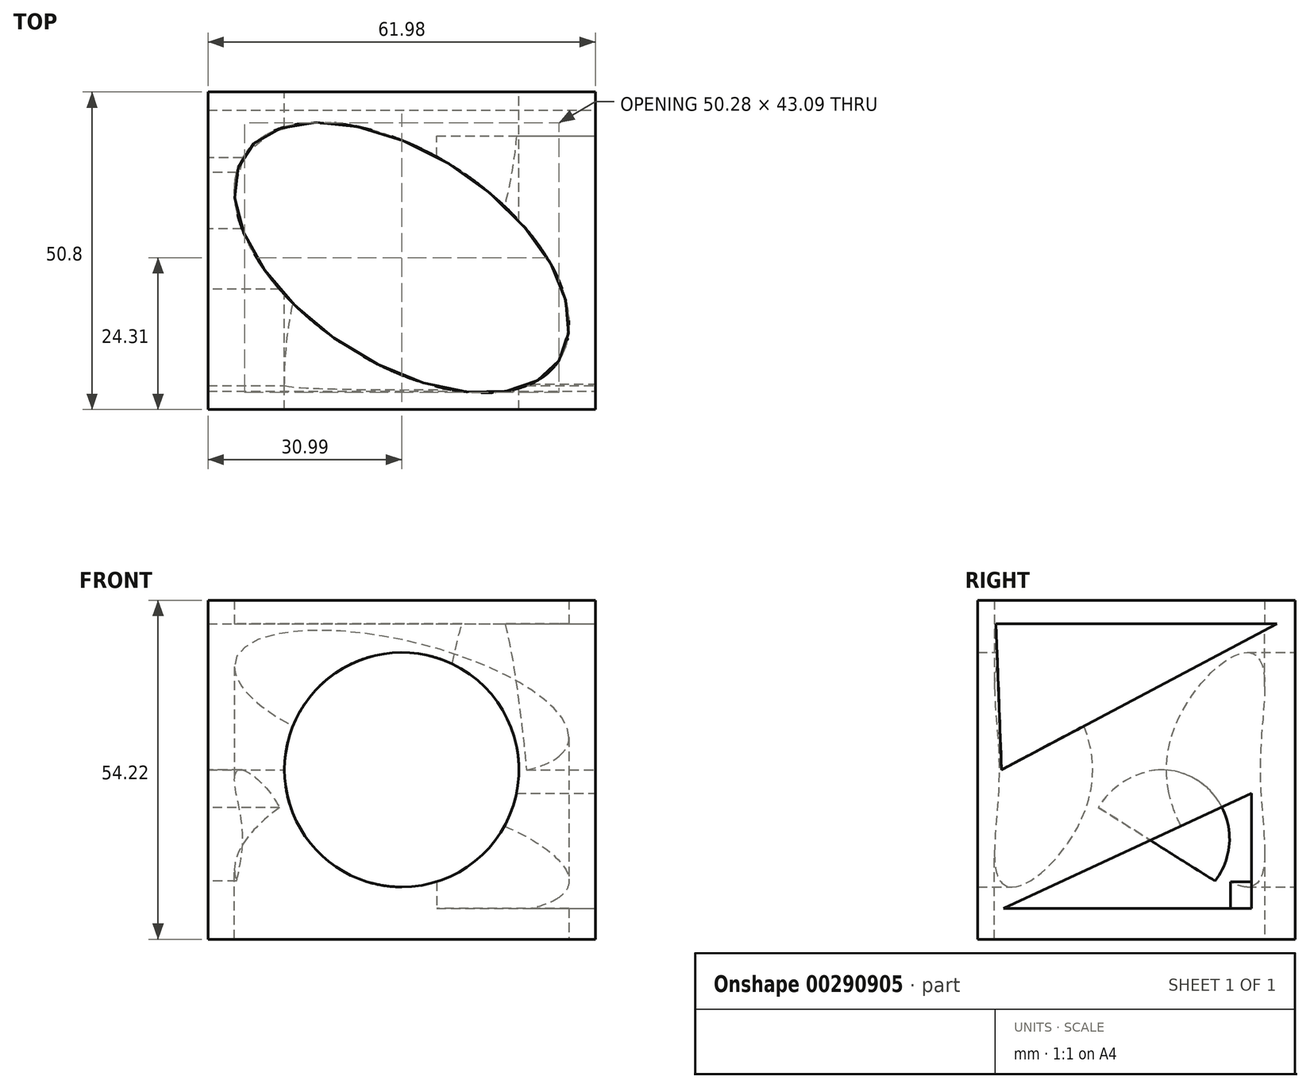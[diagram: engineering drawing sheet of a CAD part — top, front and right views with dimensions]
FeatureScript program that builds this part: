
annotation { "Feature Type Name" : "Feature", "Feature Type Description" : "" }
export const myFeature = defineFeature(function(context is Context, id is Id, definition is map)
    precondition{}
    {
        {
            var Q0;
            Q0=qCreatedBy(makeId("Front.planeOp"),FACE);
            var sketch = newSketch(context, id + "F0", { "sketchPlane" : qUnion([Q0])});
            skLineSegment(sketch, "E0.bottom", {"start": v(31, 27.1) * mm, "end": v(-31, 27.1) * mm});
            skLineSegment(sketch, "E0.top", {"start": v(31, -27.1) * mm, "end": v(-31, -27.1) * mm});
            skLineSegment(sketch, "E0.left", {"start": v(31, 27.1) * mm, "end": v(31, -27.1) * mm});
            skLineSegment(sketch, "E0.right", {"start": v(-31, 27.1) * mm, "end": v(-31, -27.1) * mm});
            skPoint(sketch, "E0.middle", {"position": v(0, 0) * mm});
            skSolve(sketch);
        }
        {
            var Q0;
            Q0 = qSketchRegion(id + "F0", true);
            extrude(context, id + "F1", {"entities" : qUnion([Q0]), "depth" : 50.8 * mm, "hasDraft" : true, "draftAngle" : 0 * degree});
        }
        {
            var Q0;
            Q0=makeQuery(id+"F1.opExtrude","CAP_FACE",FACE,{"disambiguationData":[OSD([sQuery(id+"F0.wireOp",EDGE,"E0.bottom"),sQuery(id+"F0.wireOp",EDGE,"E0.top"),sQuery(id+"F0.wireOp",EDGE,"E0.left"),sQuery(id+"F0.wireOp",EDGE,"E0.right")])],"isStart":false});
            var sketch = newSketch(context, id + "F2", { "sketchPlane" : qUnion([Q0])});
            skCircle(sketch, "E1", {"center": v(0, 0) * mm, "radius": 18.76 * mm});
            skSolve(sketch);
        }
        {
            var Q0;
            Q0 = qSketchRegion(id + "F2", true);
            extrude(context, id + "F3", {"entities" : qUnion([Q0]), "operationType" : NewBodyOperationType.REMOVE, "oppositeDirection" : true, "depth" : 50.8 * mm, "hasDraft" : true, "draftAngle" : 0 * degree});
        }
        {
            var Q0;
            Q0=makeQuery(id+"F1.opExtrude","SWEPT_FACE",FACE,{"disambiguationData":[OSD([sQuery(id+"F0.wireOp",EDGE,"E0.left")])]});
            var sketch = newSketch(context, id + "F4", { "sketchPlane" : qUnion([Q0])});
            skLineSegment(sketch, "E2", {"start": v(-47.87, 23.34) * mm, "end": v(-2.92, 23.34) * mm});
            skLineSegment(sketch, "E3", {"start": v(-2.92, 23.34) * mm, "end": v(-46.98, 0) * mm});
            skLineSegment(sketch, "E4", {"start": v(-46.98, 0) * mm, "end": v(-47.87, 23.34) * mm});
            skSolve(sketch);
        }
        {
            var Q0;
            Q0 = qSketchRegion(id + "F4", true);
            extrude(context, id + "F5", {"entities" : qUnion([Q0]), "operationType" : NewBodyOperationType.REMOVE, "oppositeDirection" : true, "depth" : 76.2 * mm, "hasDraft" : true, "draftAngle" : 0 * degree});
        }
        {
            var Q0;
            Q0=makeQuery(id+"F1.opExtrude","SWEPT_FACE",FACE,{"disambiguationData":[OSD([sQuery(id+"F0.wireOp",EDGE,"E0.left")])]});
            var sketch = newSketch(context, id + "F6", { "sketchPlane" : qUnion([Q0])});
            skLineSegment(sketch, "E5", {"start": v(-46.69, -22.18) * mm, "end": v(-7, -3.8) * mm});
            skLineSegment(sketch, "E6", {"start": v(-7, -3.8) * mm, "end": v(-7, -22.18) * mm});
            skLineSegment(sketch, "E7", {"start": v(-7, -22.18) * mm, "end": v(-46.69, -22.18) * mm});
            skSolve(sketch);
        }
        {
            var Q0;
            Q0 = qSketchRegion(id + "F6", true);
            extrude(context, id + "F7", {"entities" : qUnion([Q0]), "operationType" : NewBodyOperationType.REMOVE, "oppositeDirection" : true, "depth" : 25.4 * mm});
        }
        {
            var Q0;
            Q0=makeQuery(id+"F1.opExtrude","SWEPT_FACE",FACE,{"disambiguationData":[OSD([sQuery(id+"F0.wireOp",EDGE,"E0.right")])]});
            var sketch = newSketch(context, id + "F8", { "sketchPlane" : qUnion([Q0])});
            skArc(sketch, "E8", {"start": v(21.89, 0) * mm, "mid": v(11.7, -6.02) * mm, "end": v(12.84, -17.8) * mm});
            skArc(sketch, "E9", {"start": v(31.51, -6.02) * mm, "mid": v(27.4, -1.9) * mm, "end": v(21.89, 0) * mm});
            skPoint(sketch, "E9.startSnap0", {"position": v(11.7, -6.02) * mm});
            skLineSegment(sketch, "E10", {"start": v(12.84, -17.8) * mm, "end": v(31.51, -6.02) * mm});
            skSolve(sketch);
        }
        {
            var Q0;
            Q0 = qSketchRegion(id + "F8", true);
            extrude(context, id + "F9", {"entities" : qUnion([Q0]), "operationType" : NewBodyOperationType.REMOVE, "oppositeDirection" : true, "depth" : 25.4 * mm});
        }
        {
            var Q0;
            Q0=makeQuery(id+"F1.opExtrude","SWEPT_FACE",FACE,{"disambiguationData":[OSD([sQuery(id+"F0.wireOp",EDGE,"E0.top")])]});
            var sketch = newSketch(context, id + "F10", { "sketchPlane" : qUnion([Q0])});
            skEllipse(sketch, "E11", {"center": v(0, 26.49) * mm, "majorRadius": 30.06 * mm, "minorRadius": 16.72 * mm, "majorAxis": v(0.84, 0.55)});
            skSolve(sketch);
        }
        {
            var Q0;
            Q0 = qSketchRegion(id + "F10", true);
            extrude(context, id + "F11", {"entities" : qUnion([Q0]), "operationType" : NewBodyOperationType.REMOVE, "oppositeDirection" : true, "depth" : 76.2 * mm, "hasDraft" : true, "draftAngle" : 0 * degree});
        }
        {
            var Q0;
            Q0=qCreatedBy(makeId("Top.planeOp"),FACE);
            var sketch = newSketch(context, id + "F12", { "sketchPlane" : qUnion([Q0])});
            skLineSegment(sketch, "E12", {"start": v(0, 0) * mm, "end": v(0, 56.5) * mm});
            skLineSegment(sketch, "E13", {"start": v(0, 56.5) * mm, "end": v(-18.92, 56.5) * mm});
            skLineSegment(sketch, "E14", {"start": v(-18.92, 56.5) * mm, "end": v(-31.08, 0) * mm});
            skSolve(sketch);
        }
        {
            var Q0;
            Q0=sQuery(id+"F12.wireOp",EDGE,"E14");
            var Q1;
            Q1=sQuery(id+"F12.wireOp",EDGE,"E13");
            var Q2;
            Q2=sQuery(id+"F12.wireOp",EDGE,"E12");
            revolve(context, id + "F13", {"bodyType" : ToolBodyType.SURFACE, "surfaceEntities" : qUnion([Q0, Q1]), "axis" : qUnion([Q2]), "revolveType" : RevolveType.FULL});
        }
    });
